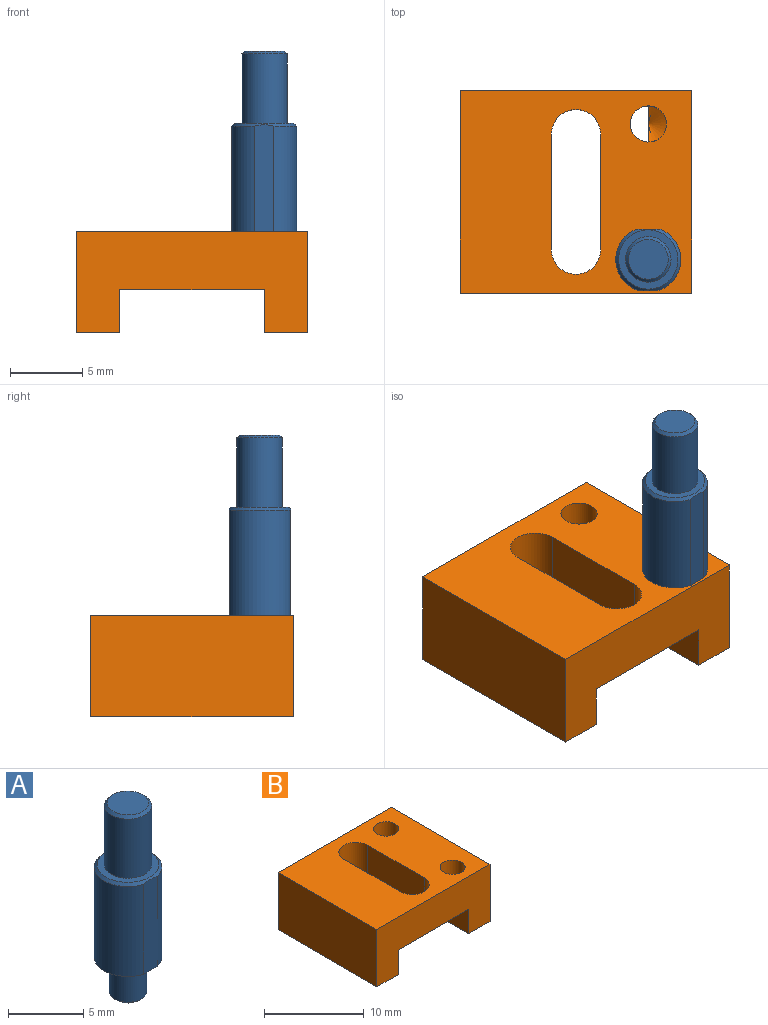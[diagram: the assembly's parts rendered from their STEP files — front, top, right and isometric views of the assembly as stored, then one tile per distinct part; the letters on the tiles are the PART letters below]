
ASSEMBLY  parts=2 mates=1
PART A: 13 faces, bbox 4.5x4.5x15.5 mm
  f0: cylinder r=2.25mm len=7.3mm, axis (0,0,-1), area 40.7mm2, adj f2,f3,f11,f12
  f1: cylinder r=2.25mm len=7.3mm, axis (0,0,-1), area 40.7mm2, adj f2,f3,f11,f12
  f2: plane 4.5x4.25mm, normal (0,0,-1), area 10.7mm2, adj f0,f1,f5,f11,f12
  f3: cone r=2.05mm half-angle=45deg, axis (0,0,-1), area 3.5mm2, adj f0,f1,f4,f11,f12
  f4: plane 4.1x4.1mm, normal (0,0,1), area 5.4mm2, adj f3,f7
  f5: cylinder r=1.25mm len=2.8mm, axis (0,0,1), area 22mm2, adj f2,f10
  f6: plane 2.1x2.1mm, normal (0,0,-1), area 3.5mm2, adj f10
  f7: cylinder r=1.57mm len=4.8mm, axis (0,0,-1), area 47.5mm2, adj f4,f9
  f8: plane 2.75x2.75mm, normal (0,0,1), area 5.9mm2, adj f9
  f9: cone r=1.38mm half-angle=45deg, axis (0,0,-1), area 2.6mm2, adj f7,f8
  f10: cone r=1.25mm half-angle=45deg, axis (0,0,1), area 2mm2, adj f5,f6
  f11: plane 7.4x1.33mm, normal (0,-1,0), area 9.8mm2, adj f0,f1,f2,f3
  f12: plane 7.45x1.62mm, normal (0,1,0), area 12mm2, adj f0,f1,f2,f3
PART B: 18 faces, bbox 16x14x7 mm
  f0: plane 14x3mm, normal (-1,0,0), area 40.1mm2, adj f6,f7,f8,f9,f10,f12
  f1: plane 14x3mm, normal (1,0,0), area 42mm2, adj f2,f7,f8,f9
  f2: plane 14x3mm, normal (0,0,-1), area 42mm2, adj f1,f3,f8,f9
  f3: plane 14x7mm, normal (-1,0,0), area 98mm2, adj f2,f4,f8,f9
  f4: plane 16x14mm, normal (0,0,1), area 177.9mm2, adj f3,f5,f8,f9,f11,f13,f14,f15
  f5: plane 14x7mm, normal (1,0,0), area 98mm2, adj f4,f6,f8,f9
  f6: plane 14x3mm, normal (0,0,-1), area 42mm2, adj f0,f5,f8,f9
  f7: plane 14x10mm, normal (0,0,-1), area 98.8mm2, adj f0,f1,f8,f9,f11,f13,f14,f15
  f8: plane 16x7mm, normal (0,1,0), area 82mm2, adj f0,f1,f2,f3,f4,f5,f6,f7
  f9: plane 16x7mm, normal (0,-1,0), area 82mm2, adj f0,f1,f2,f3,f4,f5,f6,f7
  f10: cone r=0mm half-angle=59deg, axis (0,0,1), area 2.9mm2, adj f0,f11
  f11: cylinder r=1.25mm len=4mm, axis (0,0,1), area 31.4mm2, adj f4,f7,f10
  f12: cone r=0mm half-angle=59deg, axis (0,0,1), area 2.9mm2, adj f0,f13
  f13: cylinder r=1.25mm len=4mm, axis (0,0,1), area 31.4mm2, adj f4,f7,f12
  f14: plane 8x4mm, normal (1,0,0), area 32mm2, adj f4,f7,f15,f17
  f15: cylinder r=1.7mm len=4mm, axis (0,0,1), area 21.4mm2, adj f4,f7,f14,f16
  f16: plane 8x4mm, normal (-1,0,0), area 32mm2, adj f4,f7,f15,f17
  f17: cylinder r=1.7mm len=4mm, axis (0,0,1), area 21.4mm2, adj f4,f7,f14,f16
PLACE A t=(34.58,-39.17,-10)mm
PLACE B t=(34.58,-29.78,-10)mm
MATE fastened A.f2 <-> B.f10  axis (0,0,-1) through (154.52,24.79,7.5)mm
